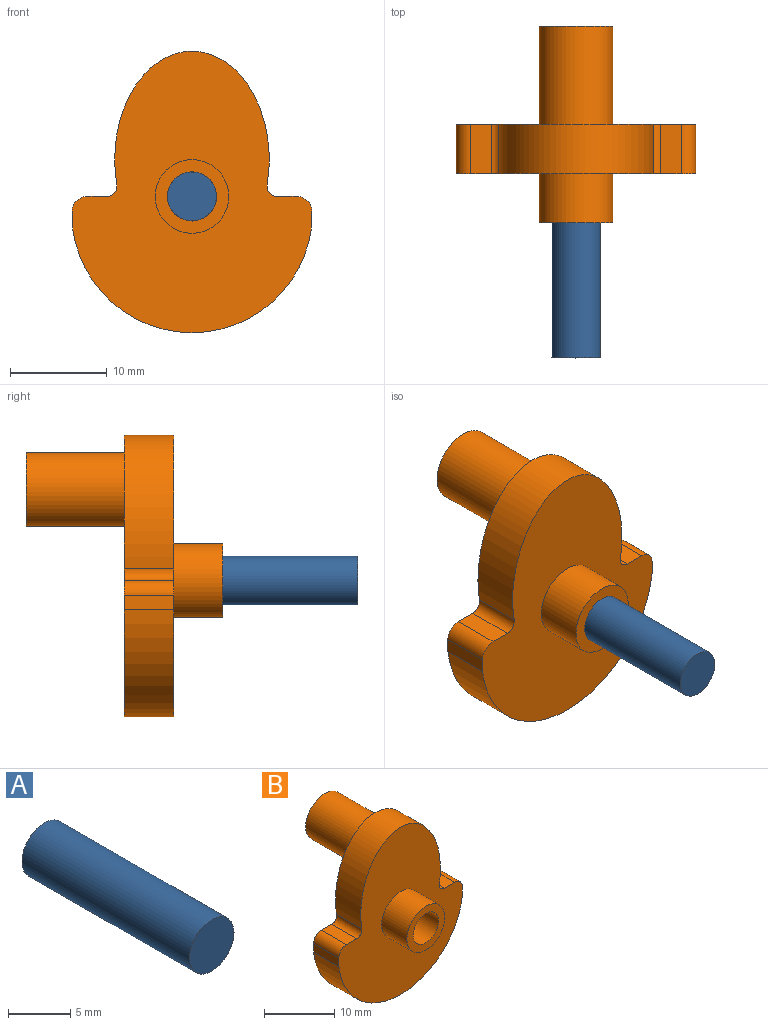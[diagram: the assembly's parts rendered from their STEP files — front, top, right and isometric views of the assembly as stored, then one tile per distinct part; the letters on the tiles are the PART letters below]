
ASSEMBLY  parts=2 mates=1
PART A: 3 faces, bbox 5.1x19.1x5.1 mm
  f0: cylinder r=2.53mm len=19.05mm, axis (0,1,0), area 302.5mm2, adj f1,f2
  f1: plane 5.05x5.05mm, normal (0,-1,0), area 20.1mm2, adj f0
  f2: plane 5.05x5.05mm, normal (0,1,0), area 20.1mm2, adj f0
PART B: 17 faces, bbox 24.8x20.3x29.1 mm
  f0: plane 5.08x1.52mm, normal (-1,0,0), area 7.7mm2, adj f2,f4,f7,f11
  f1: plane 5.08x1.52mm, normal (1,0,0), area 7.7mm2, adj f2,f4,f8,f11
  f2: plane 29.09x24.77mm, normal (0,-1,0), area 438.3mm2, adj f0,f1,f3,f5,f6,f7,f8,f9
  f3: extruded ~15.98x13.82mm, area 181mm2, adj f2,f4,f9,f10
  f4: plane 29.09x24.77mm, normal (0,1,0), area 418mm2, adj f0,f1,f3,f5,f6,f7,f8,f9
  f5: plane 5.08x2.09mm, normal (0,0,1), area 10.6mm2, adj f2,f4,f7,f9
  f6: plane 5.08x2.09mm, normal (0,0,1), area 10.6mm2, adj f2,f4,f8,f10
  f7: cylinder r=1.52mm len=5.08mm, axis (0,1,0), area 12.2mm2, adj f0,f2,f4,f5
  f8: cylinder r=1.52mm len=5.08mm, axis (0,-1,0), area 12.2mm2, adj f1,f2,f4,f6
  f9: cylinder r=1.02mm len=5.08mm, axis (0,1,0), area 9mm2, adj f2,f3,f4,f5
  f10: cylinder r=1.02mm len=5.08mm, axis (0,1,0), area 9mm2, adj f2,f3,f4,f6
  f11: cylinder r=12.46mm len=24.77mm, axis (0,1,0), area 184.4mm2, adj f0,f1,f2,f4
  f12: cylinder r=3.81mm len=10.16mm, axis (0,-1,0), area 243.2mm2, adj f4,f13
  f13: plane 7.62x7.62mm, normal (0,1,0), area 45.6mm2, adj f12
  f14: plane 7.62x7.62mm, normal (0,-1,0), area 25.3mm2, adj f15,f16
  f15: cylinder r=3.81mm len=7.62mm, axis (0,-1,0), area 121.6mm2, adj f2,f14
  f16: cylinder r=2.54mm len=10.16mm, axis (0,-1,0), area 162.1mm2, adj f4,f14
PLACE A t=(-21.7,-15.54,4.02)mm
PLACE B t=(-21.7,-10.46,4.02)mm
MATE revolute A.f0 <-> B.f15  axis (0,1,0) through (-21.7,-15.54,4.02)mm
